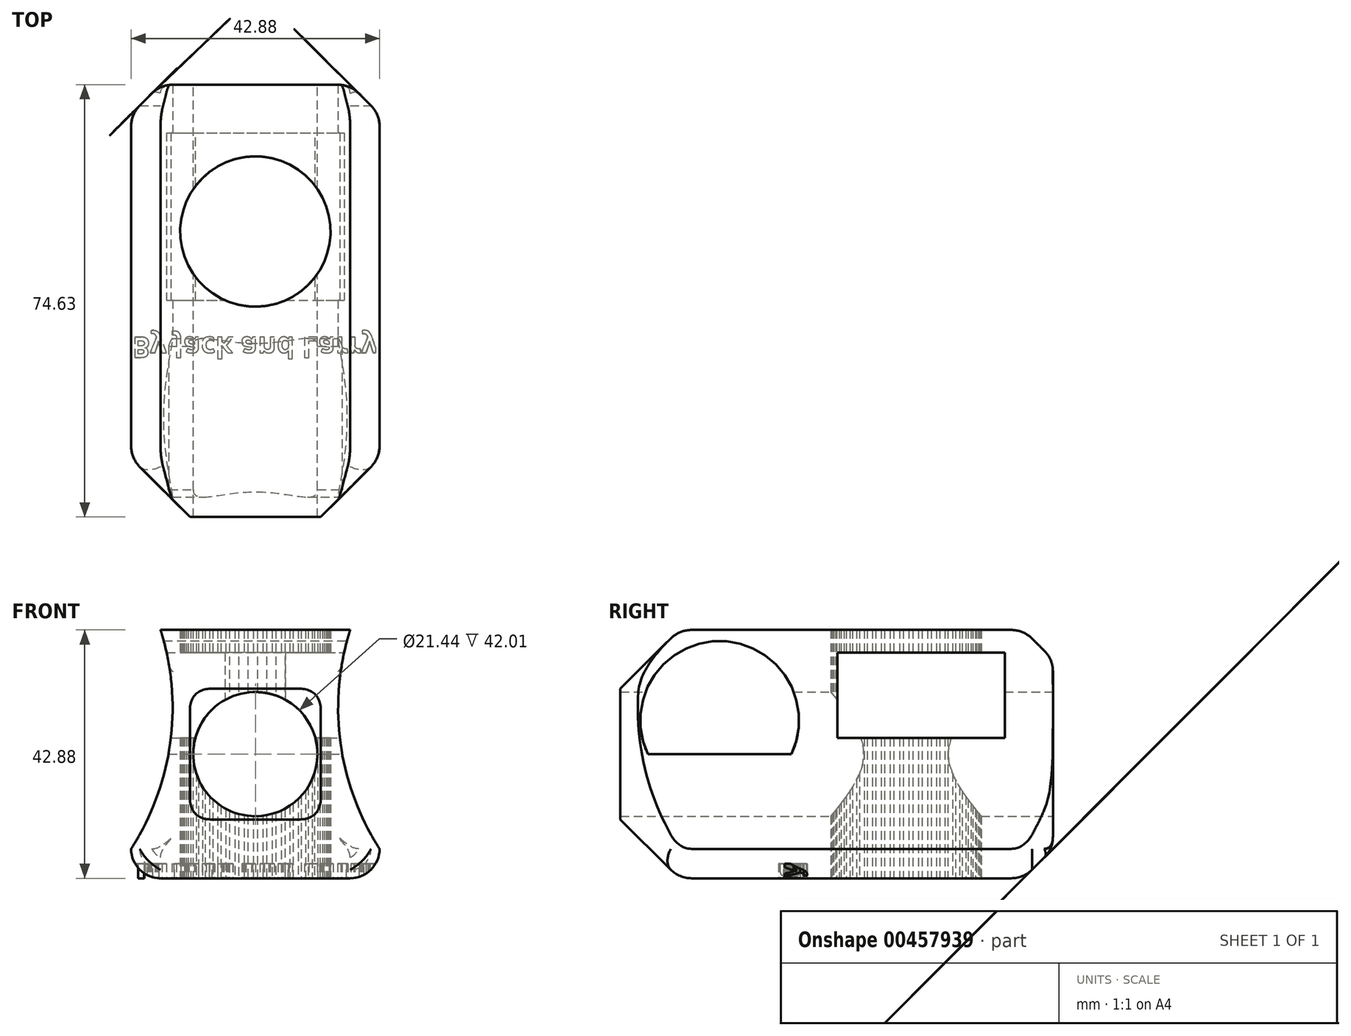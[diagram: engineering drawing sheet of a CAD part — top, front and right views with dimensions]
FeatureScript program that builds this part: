
annotation { "Feature Type Name" : "Feature", "Feature Type Description" : "" }
export const myFeature = defineFeature(function(context is Context, id is Id, definition is map)
    precondition{}
    {
        {
            var Q0;
            Q0=qCreatedBy(makeId("Front.planeOp"),FACE);
            var sketch = newSketch(context, id + "F0", { "sketchPlane" : qUnion([Q0])});
            skLineSegment(sketch, "E0.bottom", {"start": v(-21.44, 21.44) * mm, "end": v(21.44, 21.44) * mm});
            skLineSegment(sketch, "E0.top", {"start": v(-21.44, -21.44) * mm, "end": v(21.44, -21.44) * mm});
            skLineSegment(sketch, "E0.left", {"start": v(-21.44, 21.44) * mm, "end": v(-21.44, -21.44) * mm});
            skLineSegment(sketch, "E0.right", {"start": v(21.44, 21.44) * mm, "end": v(21.44, -21.44) * mm});
            skPoint(sketch, "E0.middle", {"position": v(0, 0) * mm});
            skCircle(sketch, "E1", {"center": v(0, 0) * mm, "radius": 10.72 * mm});
            skSolve(sketch);
        }
        {
            var Q0;
            Q0=makeQuery(id+"F0.imprint","IMPRINT",FACE,{"disambiguationData":[TD([[makeQuery(id+"F0.imprint","IMPRINT",EDGE,{"derivedFrom":sQuery(id+"F0.wireOp",EDGE,"E0.bottom")}),-1.0]])]});
            extrude(context, id + "F1", {"entities" : qUnion([Q0]), "depth" : 74.63 * mm, "offsetDistance" : 25.4 * mm});
        }
        {
            var Q0;
            Q0=makeQuery(id+"F1.opExtrude","SWEPT_FACE",FACE,{"disambiguationData":[OSD([sQuery(id+"F0.wireOp",EDGE,"E0.top")])]});
            var sketch = newSketch(context, id + "F2", { "sketchPlane" : qUnion([Q0])});
            skText(sketch, "E2", { "text": "By Jack and Larry", "fontName": "OpenSans-Bold.ttf"});
            const initialGuessF2  = {"E2": [-0.02144, 0.04357, 1, 0, 0.00355]};
            skSetInitialGuess(sketch, initialGuessF2);
            skSolve(sketch);
        }
        {
            var Q0;
            Q0 = qSketchRegion(id + "F2", true);
            extrude(context, id + "F3", {"entities" : qUnion([Q0]), "operationType" : NewBodyOperationType.REMOVE, "oppositeDirection" : true, "depth" : 2.54 * mm, "offsetDistance" : 25.4 * mm});
        }
        {
            var Q0;
            Q0=makeQuery(id+"F1.opExtrude","CAP_EDGE",EDGE,{"disambiguationData":[OSD([sQuery(id+"F0.wireOp",EDGE,"E0.top")])],"isStart":false});
            var Q1;
            Q1=makeQuery(id+"F1.opExtrude","CAP_EDGE",EDGE,{"disambiguationData":[OSD([sQuery(id+"F0.wireOp",EDGE,"E0.right")])],"isStart":false});
            var Q2;
            Q2=makeQuery(id+"F1.opExtrude","CAP_EDGE",EDGE,{"disambiguationData":[OSD([sQuery(id+"F0.wireOp",EDGE,"E0.left")])],"isStart":false});
            var Q3;
            Q3=makeQuery(id+"F1.opExtrude","CAP_EDGE",EDGE,{"disambiguationData":[OSD([sQuery(id+"F0.wireOp",EDGE,"E0.bottom")])],"isStart":false});
            chamfer(context, id + "F4", {"entities" : qUnion([Q0, Q1, Q2, Q3]), "width" : 10.16 * mm, "tangentPropagation" : true});
        }
        {
            var Q0;
            {var subQ0=sQuery(id+"F0.wireOp",EDGE,"E0.left");var subQ3=sQuery(id+"F0.wireOp",EDGE,"E0.top");Q0=makeQuery(id+"F4.opChamfer","BLEND_EDGE",EDGE,{"blendedFrom":[makeQuery(id+"F1.opExtrude","CAP_EDGE",EDGE,{"disambiguationData":[OSD([subQ3])],"isStart":false}),makeQuery(id+"F3.boolean.opBoolean","SPLIT",FACE,{"disambiguationData":[TD([makeQuery(id+"F1.opExtrude","SWEPT_FACE",FACE,{"disambiguationData":[OSD([subQ0])]})])],"derivedFrom":makeQuery(id+"F1.opExtrude","SWEPT_FACE",FACE,{"disambiguationData":[OSD([subQ3])]})})],"blendedInto":[makeQuery(id+"F3.boolean.opBoolean","SPLIT",FACE,{"disambiguationData":[TD([makeQuery(id+"F1.opExtrude","SWEPT_FACE",FACE,{"disambiguationData":[OSD([subQ0])]})])],"derivedFrom":makeQuery(id+"F1.opExtrude","SWEPT_FACE",FACE,{"disambiguationData":[OSD([subQ3])]})})]});}
            var Q1;
            {var subQ0=sQuery(id+"F0.wireOp",EDGE,"E0.right");Q1=makeQuery(id+"F4.opChamfer","BLEND_EDGE",EDGE,{"blendedFrom":[makeQuery(id+"F1.opExtrude","CAP_EDGE",EDGE,{"disambiguationData":[OSD([subQ0])],"isStart":false}),makeQuery(id+"F1.opExtrude","SWEPT_FACE",FACE,{"disambiguationData":[OSD([subQ0])]})],"blendedInto":[makeQuery(id+"F1.opExtrude","SWEPT_FACE",FACE,{"disambiguationData":[OSD([subQ0])]})]});}
            var Q2;
            {var subQ0=sQuery(id+"F0.wireOp",EDGE,"E0.left");Q2=makeQuery(id+"F4.opChamfer","BLEND_EDGE",EDGE,{"blendedFrom":[makeQuery(id+"F1.opExtrude","CAP_EDGE",EDGE,{"disambiguationData":[OSD([subQ0])],"isStart":false}),makeQuery(id+"F1.opExtrude","SWEPT_FACE",FACE,{"disambiguationData":[OSD([subQ0])]})],"blendedInto":[makeQuery(id+"F1.opExtrude","SWEPT_FACE",FACE,{"disambiguationData":[OSD([subQ0])]})]});}
            var Q3;
            {var subQ0=sQuery(id+"F0.wireOp",EDGE,"E0.left");var subQ4=sQuery(id+"F0.wireOp",EDGE,"E0.bottom");Q3=makeQuery(id+"F4.opChamfer","BLEND_EDGE",EDGE,{"blendedFrom":[makeQuery(id+"F1.opExtrude","CAP_EDGE",EDGE,{"disambiguationData":[OSD([subQ4])],"isStart":false}),makeQuery(id+"F3.boolean.opBoolean","SPLIT",FACE,{"disambiguationData":[TD([makeQuery(id+"F1.opExtrude","SWEPT_FACE",FACE,{"disambiguationData":[OSD([subQ0])]})])],"derivedFrom":makeQuery(id+"F1.opExtrude","SWEPT_FACE",FACE,{"disambiguationData":[OSD([subQ4])]})})],"blendedInto":[makeQuery(id+"F3.boolean.opBoolean","SPLIT",FACE,{"disambiguationData":[TD([makeQuery(id+"F1.opExtrude","SWEPT_FACE",FACE,{"disambiguationData":[OSD([subQ0])]})])],"derivedFrom":makeQuery(id+"F1.opExtrude","SWEPT_FACE",FACE,{"disambiguationData":[OSD([subQ4])]})})]});}
            fillet(context, id + "F5", {"entities" : qUnion([Q0, Q1, Q2, Q3]), "radius" : 5.08 * mm, "tangentPropagation" : true, "allowEdgeOverflow" : false});
        }
        {
            var Q0;
            Q0=makeQuery(id+"F4.opChamfer","BLEND_EDGE",EDGE,{"blendedFrom":[makeQuery(id+"F1.opExtrude","CAP_EDGE",EDGE,{"disambiguationData":[OSD([sQuery(id+"F0.wireOp",EDGE,"E0.top")])],"isStart":false}),makeQuery(id+"F1.opExtrude","CAP_EDGE",EDGE,{"disambiguationData":[OSD([sQuery(id+"F0.wireOp",EDGE,"E0.right")])],"isStart":false})],"blendedInto":[]});
            var Q1;
            Q1=makeQuery(id+"F4.opChamfer","BLEND_EDGE",EDGE,{"blendedFrom":[makeQuery(id+"F1.opExtrude","CAP_EDGE",EDGE,{"disambiguationData":[OSD([sQuery(id+"F0.wireOp",EDGE,"E0.top")])],"isStart":false}),makeQuery(id+"F1.opExtrude","CAP_EDGE",EDGE,{"disambiguationData":[OSD([sQuery(id+"F0.wireOp",EDGE,"E0.left")])],"isStart":false})],"blendedInto":[]});
            var Q2;
            Q2=makeQuery(id+"F4.opChamfer","BLEND_EDGE",EDGE,{"blendedFrom":[makeQuery(id+"F1.opExtrude","CAP_EDGE",EDGE,{"disambiguationData":[OSD([sQuery(id+"F0.wireOp",EDGE,"E0.bottom")])],"isStart":false}),makeQuery(id+"F1.opExtrude","CAP_EDGE",EDGE,{"disambiguationData":[OSD([sQuery(id+"F0.wireOp",EDGE,"E0.right")])],"isStart":false})],"blendedInto":[]});
            var Q3;
            Q3=makeQuery(id+"F4.opChamfer","BLEND_EDGE",EDGE,{"blendedFrom":[makeQuery(id+"F1.opExtrude","CAP_EDGE",EDGE,{"disambiguationData":[OSD([sQuery(id+"F0.wireOp",EDGE,"E0.bottom")])],"isStart":false}),makeQuery(id+"F1.opExtrude","CAP_EDGE",EDGE,{"disambiguationData":[OSD([sQuery(id+"F0.wireOp",EDGE,"E0.left")])],"isStart":false})],"blendedInto":[]});
            fillet(context, id + "F6", {"entities" : qUnion([Q0, Q1, Q2, Q3]), "radius" : 5.08 * mm, "tangentPropagation" : true, "allowEdgeOverflow" : false});
        }
        {
            var Q0;
            Q0=makeQuery(id+"F1.opExtrude","CAP_EDGE",EDGE,{"disambiguationData":[OSD([sQuery(id+"F0.wireOp",EDGE,"E0.top")])],"isStart":true});
            chamfer(context, id + "F7", {"entities" : qUnion([Q0]), "width" : 5.08 * mm, "tangentPropagation" : true});
        }
        {
            var Q0;
            {var subQ0=sQuery(id+"F0.wireOp",EDGE,"E1");var subQ1=sQuery(id+"F0.wireOp",EDGE,"E0.right");var subQ2=sQuery(id+"F0.wireOp",EDGE,"E0.left");var subQ3=sQuery(id+"F0.wireOp",EDGE,"E0.top");var subQ4=sQuery(id+"F0.wireOp",EDGE,"E0.bottom");Q0=makeQuery(id+"F7.opChamfer","BLEND_FACE",FACE,{"disambiguationData":[OSD([subQ4,subQ3,subQ2,subQ1,subQ0]),TDD([makeQuery(id+"F6.opFillet","BLEND_EDGE",EDGE,{"blendedFrom":[makeQuery(id+"F1.opExtrude","SWEPT_EDGE",EDGE,{"disambiguationData":[OSD([subQ3,subQ2])]}),makeQuery(id+"F1.opExtrude","CAP_FACE",FACE,{"disambiguationData":[OSD([subQ4,subQ3,subQ2,subQ1,subQ0])],"isStart":true})],"blendedInto":[makeQuery(id+"F1.opExtrude","CAP_FACE",FACE,{"disambiguationData":[OSD([subQ4,subQ3,subQ2,subQ1,subQ0])],"isStart":true})]})])]});}
            var Q1;
            {var subQ0=sQuery(id+"F0.wireOp",EDGE,"E1");var subQ1=sQuery(id+"F0.wireOp",EDGE,"E0.right");var subQ2=sQuery(id+"F0.wireOp",EDGE,"E0.left");var subQ3=sQuery(id+"F0.wireOp",EDGE,"E0.top");var subQ4=sQuery(id+"F0.wireOp",EDGE,"E0.bottom");Q1=makeQuery(id+"F7.opChamfer","BLEND_FACE",FACE,{"disambiguationData":[OSD([subQ4,subQ3,subQ2,subQ1,subQ0]),TDD([makeQuery(id+"F6.opFillet","BLEND_EDGE",EDGE,{"blendedFrom":[makeQuery(id+"F1.opExtrude","SWEPT_EDGE",EDGE,{"disambiguationData":[OSD([subQ3,subQ1])]}),makeQuery(id+"F1.opExtrude","CAP_FACE",FACE,{"disambiguationData":[OSD([subQ4,subQ3,subQ2,subQ1,subQ0])],"isStart":true})],"blendedInto":[makeQuery(id+"F1.opExtrude","CAP_FACE",FACE,{"disambiguationData":[OSD([subQ4,subQ3,subQ2,subQ1,subQ0])],"isStart":true})]})])]});}
            var Q2;
            {var subQ0=sQuery(id+"F0.wireOp",EDGE,"E1");var subQ1=sQuery(id+"F0.wireOp",EDGE,"E0.right");var subQ2=sQuery(id+"F0.wireOp",EDGE,"E0.left");var subQ3=sQuery(id+"F0.wireOp",EDGE,"E0.top");var subQ4=sQuery(id+"F0.wireOp",EDGE,"E0.bottom");Q2=makeQuery(id+"F7.opChamfer","BLEND_FACE",FACE,{"disambiguationData":[OSD([subQ4,subQ3,subQ2,subQ1,subQ0]),TDD([makeQuery(id+"F6.opFillet","BLEND_EDGE",EDGE,{"blendedFrom":[makeQuery(id+"F1.opExtrude","SWEPT_EDGE",EDGE,{"disambiguationData":[OSD([subQ4,subQ2])]}),makeQuery(id+"F1.opExtrude","CAP_FACE",FACE,{"disambiguationData":[OSD([subQ4,subQ3,subQ2,subQ1,subQ0])],"isStart":true})],"blendedInto":[makeQuery(id+"F1.opExtrude","CAP_FACE",FACE,{"disambiguationData":[OSD([subQ4,subQ3,subQ2,subQ1,subQ0])],"isStart":true})]})])]});}
            var Q3;
            {var subQ0=sQuery(id+"F0.wireOp",EDGE,"E1");var subQ1=sQuery(id+"F0.wireOp",EDGE,"E0.right");var subQ2=sQuery(id+"F0.wireOp",EDGE,"E0.left");var subQ3=sQuery(id+"F0.wireOp",EDGE,"E0.top");var subQ4=sQuery(id+"F0.wireOp",EDGE,"E0.bottom");Q3=makeQuery(id+"F7.opChamfer","BLEND_FACE",FACE,{"disambiguationData":[OSD([subQ4,subQ3,subQ2,subQ1,subQ0]),TDD([makeQuery(id+"F6.opFillet","BLEND_EDGE",EDGE,{"blendedFrom":[makeQuery(id+"F1.opExtrude","SWEPT_EDGE",EDGE,{"disambiguationData":[OSD([subQ4,subQ1])]}),makeQuery(id+"F1.opExtrude","CAP_FACE",FACE,{"disambiguationData":[OSD([subQ4,subQ3,subQ2,subQ1,subQ0])],"isStart":true})],"blendedInto":[makeQuery(id+"F1.opExtrude","CAP_FACE",FACE,{"disambiguationData":[OSD([subQ4,subQ3,subQ2,subQ1,subQ0])],"isStart":true})]})])]});}
            var Q4;
            Q4=makeQuery(id+"F7.opChamfer","BLEND_FACE",FACE,{"disambiguationData":[OSD([sQuery(id+"F0.wireOp",EDGE,"E0.right")])]});
            var Q5;
            Q5=makeQuery(id+"F7.opChamfer","BLEND_FACE",FACE,{"disambiguationData":[OSD([sQuery(id+"F0.wireOp",EDGE,"E0.left")])]});
            var Q6;
            Q6=makeQuery(id+"F7.opChamfer","BLEND_FACE",FACE,{"disambiguationData":[OSD([sQuery(id+"F0.wireOp",EDGE,"E0.bottom")])]});
            var Q7;
            Q7=makeQuery(id+"F7.opChamfer","BLEND_FACE",FACE,{"disambiguationData":[OSD([sQuery(id+"F0.wireOp",EDGE,"E0.top")])]});
            fillet(context, id + "F8", {"entities" : qUnion([Q0, Q1, Q2, Q3, Q4, Q5, Q6, Q7]), "radius" : 5.08 * mm, "tangentPropagation" : true, "allowEdgeOverflow" : false});
        }
        {
            var Q0;
            Q0=makeQuery(id+"F1.opExtrude","CAP_FACE",FACE,{"disambiguationData":[OSD([sQuery(id+"F0.wireOp",EDGE,"E0.bottom"),sQuery(id+"F0.wireOp",EDGE,"E0.top"),sQuery(id+"F0.wireOp",EDGE,"E0.left"),sQuery(id+"F0.wireOp",EDGE,"E0.right"),sQuery(id+"F0.wireOp",EDGE,"E1")])],"isStart":false});
            var sketch = newSketch(context, id + "F9", { "sketchPlane" : qUnion([Q0])});
            skLineSegment(sketch, "E3.0", {"start": v(21.44, 16.36) * mm, "end": v(21.44, -16.36) * mm});
            skLineSegment(sketch, "E4.0", {"start": v(-21.44, -16.36) * mm, "end": v(-21.44, 16.36) * mm});
            skArc(sketch, "E5.0", {"start": v(16.36, 21.44) * mm, "mid": v(19.95, 19.95) * mm, "end": v(21.44, 16.36) * mm});
            skLineSegment(sketch, "E6.0", {"start": v(-16.36, 21.44) * mm, "end": v(16.36, 21.44) * mm});
            skArc(sketch, "E7.0", {"start": v(-21.44, 16.36) * mm, "mid": v(-19.95, 19.95) * mm, "end": v(-16.36, 21.44) * mm});
            skArc(sketch, "E8", {"start": v(16.36, 21.44) * mm, "mid": v(14.68, 1.97) * mm, "end": v(21.44, -16.36) * mm});
            skArc(sketch, "E9.MirrorCS", {"start": v(-16.36, 21.44) * mm, "mid": v(-14.68, 1.97) * mm, "end": v(-21.44, -16.36) * mm});
            skSolve(sketch);
        }
        {
            var Q0;
            Q0=makeQuery(id+"F9.imprint","IMPRINT",FACE,{"disambiguationData":[TD([[makeQuery(id+"F9.imprint","IMPRINT",EDGE,{"derivedFrom":sQuery(id+"F9.wireOp",EDGE,"E4.0")}),-1.0]])]});
            var Q1;
            Q1=makeQuery(id+"F9.imprint","IMPRINT",FACE,{"disambiguationData":[TD([[makeQuery(id+"F9.imprint","IMPRINT",EDGE,{"derivedFrom":sQuery(id+"F9.wireOp",EDGE,"E3.0")}),-1.0]])]});
            extrude(context, id + "F10", {"entities" : qUnion([Q0, Q1]), "operationType" : NewBodyOperationType.REMOVE, "oppositeDirection" : true, "depth" : 76.2 * mm, "offsetDistance" : 25.4 * mm});
        }
        {
            var Q0;
            Q0=makeQuery(id+"F10.boolean.opBoolean","COPY",FACE,{"derivedFrom":makeQuery(id+"F10.opExtrude","SWEPT_FACE",FACE,{"disambiguationData":[OSD([sQuery(id+"F9.wireOp",EDGE,"E8")])]})});
            cPlane(context, id + "F11", {"entities" : qUnion([Q0]), "cplaneType" : CPlaneType.LINE_ANGLE, "offset" : 25.4 * mm, "angle" : 90 * degree, "oppositeDirection" : true, "width" : 152.4 * mm, "height" : 152.4 * mm});
        }
        {
            var Q0;
            Q0=qCreatedBy(id+"F11.planeOp",FACE);
            var sketch = newSketch(context, id + "F12", { "sketchPlane" : qUnion([Q0])});
            skLineSegment(sketch, "E10.bottom", {"start": v(37.2, 2.82) * mm, "end": v(8.3, 2.82) * mm});
            skLineSegment(sketch, "E10.top", {"start": v(37.2, 17.52) * mm, "end": v(8.3, 17.52) * mm});
            skLineSegment(sketch, "E10.left", {"start": v(37.2, 2.82) * mm, "end": v(37.2, 17.52) * mm});
            skLineSegment(sketch, "E10.right", {"start": v(8.3, 2.82) * mm, "end": v(8.3, 17.52) * mm});
            skLineSegment(sketch, "E11", {"start": v(69.89, 0) * mm, "end": v(45.13, 0) * mm});
            skArc(sketch, "E12", {"start": v(69.89, 0) * mm, "mid": v(57.5, 19.53) * mm, "end": v(45.13, 0) * mm});
            skSolve(sketch);
        }
        {
            var Q0;
            Q0 = qSketchRegion(id + "F12", true);
            extrude(context, id + "F13", {"entities" : qUnion([Q0]), "operationType" : NewBodyOperationType.REMOVE, "depth" : 113.8 * mm, "offsetDistance" : 25.4 * mm});
        }
        {
            var Q0;
            {var subQ0=sQuery(id+"F0.wireOp",EDGE,"E0.left");var subQ3=sQuery(id+"F0.wireOp",EDGE,"E0.top");Q0=makeQuery(id+"F3.boolean.opBoolean","SPLIT",FACE,{"disambiguationData":[TD([makeQuery(id+"F1.opExtrude","SWEPT_FACE",FACE,{"disambiguationData":[OSD([subQ0])]})])],"derivedFrom":makeQuery(id+"F1.opExtrude","SWEPT_FACE",FACE,{"disambiguationData":[OSD([subQ3])]})});}
            var sketch = newSketch(context, id + "F14", { "sketchPlane" : qUnion([Q0])});
            skCircle(sketch, "E13.cCircle", {"center": v(0, 25.34) * mm, "radius": 12.96 * mm, "construction": true});
            skPoint(sketch, "E13.cCircle.centerSnap0", {"position": v(-16.36, 25.34) * mm});
            skLineSegment(sketch, "E13.0", {"start": v(-7.37, 36.03) * mm, "end": v(-5.97, 36.87) * mm});
            skLineSegment(sketch, "E13.1", {"start": v(-5.97, 36.87) * mm, "end": v(-4.48, 37.52) * mm});
            skLineSegment(sketch, "E13.2", {"start": v(-4.48, 37.52) * mm, "end": v(-2.91, 37.99) * mm});
            skLineSegment(sketch, "E13.3", {"start": v(-2.91, 37.99) * mm, "end": v(-1.3, 38.25) * mm});
            skLineSegment(sketch, "E13.4", {"start": v(-1.3, 38.25) * mm, "end": v(0.32, 38.32) * mm});
            skLineSegment(sketch, "E13.5", {"start": v(0.32, 38.32) * mm, "end": v(1.95, 38.17) * mm});
            skLineSegment(sketch, "E13.6", {"start": v(1.95, 38.17) * mm, "end": v(3.54, 37.83) * mm});
            skLineSegment(sketch, "E13.7", {"start": v(3.54, 37.83) * mm, "end": v(5.08, 37.29) * mm});
            skLineSegment(sketch, "E13.8", {"start": v(5.08, 37.29) * mm, "end": v(6.54, 36.55) * mm});
            skLineSegment(sketch, "E13.9", {"start": v(6.54, 36.55) * mm, "end": v(7.9, 35.65) * mm});
            skLineSegment(sketch, "E13.10", {"start": v(7.9, 35.65) * mm, "end": v(9.12, 34.58) * mm});
            skLineSegment(sketch, "E13.11", {"start": v(9.12, 34.58) * mm, "end": v(10.2, 33.36) * mm});
            skLineSegment(sketch, "E13.12", {"start": v(10.2, 33.36) * mm, "end": v(11.13, 32.02) * mm});
            skLineSegment(sketch, "E13.13", {"start": v(11.13, 32.02) * mm, "end": v(11.88, 30.57) * mm});
            skLineSegment(sketch, "E13.14", {"start": v(11.88, 30.57) * mm, "end": v(12.44, 29.04) * mm});
            skLineSegment(sketch, "E13.15", {"start": v(12.44, 29.04) * mm, "end": v(12.8, 27.45) * mm});
            skLineSegment(sketch, "E13.16", {"start": v(12.8, 27.45) * mm, "end": v(12.97, 25.83) * mm});
            skLineSegment(sketch, "E13.17", {"start": v(12.97, 25.83) * mm, "end": v(12.93, 24.2) * mm});
            skLineSegment(sketch, "E13.18", {"start": v(12.93, 24.2) * mm, "end": v(12.69, 22.59) * mm});
            skLineSegment(sketch, "E13.19", {"start": v(12.69, 22.59) * mm, "end": v(12.24, 21.02) * mm});
            skLineSegment(sketch, "E13.20", {"start": v(12.24, 21.02) * mm, "end": v(11.6, 19.52) * mm});
            skLineSegment(sketch, "E13.21", {"start": v(11.6, 19.52) * mm, "end": v(10.78, 18.11) * mm});
            skLineSegment(sketch, "E13.22", {"start": v(10.78, 18.11) * mm, "end": v(9.8, 16.82) * mm});
            skLineSegment(sketch, "E13.23", {"start": v(9.8, 16.82) * mm, "end": v(8.65, 15.66) * mm});
            skLineSegment(sketch, "E13.24", {"start": v(8.65, 15.66) * mm, "end": v(7.37, 14.65) * mm});
            skLineSegment(sketch, "E13.25", {"start": v(7.37, 14.65) * mm, "end": v(5.97, 13.8) * mm});
            skLineSegment(sketch, "E13.26", {"start": v(5.97, 13.8) * mm, "end": v(4.48, 13.15) * mm});
            skLineSegment(sketch, "E13.27", {"start": v(4.48, 13.15) * mm, "end": v(2.91, 12.69) * mm});
            skLineSegment(sketch, "E13.28", {"start": v(2.91, 12.69) * mm, "end": v(1.3, 12.42) * mm});
            skLineSegment(sketch, "E13.29", {"start": v(1.3, 12.42) * mm, "end": v(-0.32, 12.36) * mm});
            skLineSegment(sketch, "E13.30", {"start": v(-0.32, 12.36) * mm, "end": v(-1.95, 12.5) * mm});
            skLineSegment(sketch, "E13.31", {"start": v(-1.95, 12.5) * mm, "end": v(-3.54, 12.85) * mm});
            skLineSegment(sketch, "E13.32", {"start": v(-3.54, 12.85) * mm, "end": v(-5.08, 13.4) * mm});
            skLineSegment(sketch, "E13.33", {"start": v(-5.08, 13.4) * mm, "end": v(-6.54, 14.12) * mm});
            skLineSegment(sketch, "E13.34", {"start": v(-6.54, 14.12) * mm, "end": v(-7.9, 15.03) * mm});
            skLineSegment(sketch, "E13.35", {"start": v(-7.9, 15.03) * mm, "end": v(-9.12, 16.1) * mm});
            skLineSegment(sketch, "E13.36", {"start": v(-9.12, 16.1) * mm, "end": v(-10.2, 17.32) * mm});
            skLineSegment(sketch, "E13.37", {"start": v(-10.2, 17.32) * mm, "end": v(-11.13, 18.66) * mm});
            skLineSegment(sketch, "E13.38", {"start": v(-11.13, 18.66) * mm, "end": v(-11.88, 20.1) * mm});
            skLineSegment(sketch, "E13.39", {"start": v(-11.88, 20.1) * mm, "end": v(-12.44, 21.64) * mm});
            skLineSegment(sketch, "E13.40", {"start": v(-12.44, 21.64) * mm, "end": v(-12.8, 23.22) * mm});
            skLineSegment(sketch, "E13.41", {"start": v(-12.8, 23.22) * mm, "end": v(-12.97, 24.85) * mm});
            skLineSegment(sketch, "E13.42", {"start": v(-12.97, 24.85) * mm, "end": v(-12.93, 26.48) * mm});
            skLineSegment(sketch, "E13.43", {"start": v(-12.93, 26.48) * mm, "end": v(-12.69, 28.09) * mm});
            skLineSegment(sketch, "E13.44", {"start": v(-12.69, 28.09) * mm, "end": v(-12.24, 29.66) * mm});
            skLineSegment(sketch, "E13.45", {"start": v(-12.24, 29.66) * mm, "end": v(-11.6, 31.16) * mm});
            skLineSegment(sketch, "E13.46", {"start": v(-11.6, 31.16) * mm, "end": v(-10.78, 32.57) * mm});
            skLineSegment(sketch, "E13.47", {"start": v(-10.78, 32.57) * mm, "end": v(-9.8, 33.86) * mm});
            skLineSegment(sketch, "E13.48", {"start": v(-9.8, 33.86) * mm, "end": v(-8.65, 35.02) * mm});
            skLineSegment(sketch, "E13.49", {"start": v(-8.65, 35.02) * mm, "end": v(-7.37, 36.03) * mm});
            skPoint(sketch, "E13.0.midPoint", {"position": v(-6.67, 36.45) * mm});
            skSolve(sketch);
        }
        {
            var Q0;
            Q0 = qSketchRegion(id + "F14", true);
            extrude(context, id + "F15", {"entities" : qUnion([Q0]), "operationType" : NewBodyOperationType.REMOVE, "oppositeDirection" : true, "depth" : 76.2 * mm, "offsetDistance" : 25.4 * mm});
        }
    });
